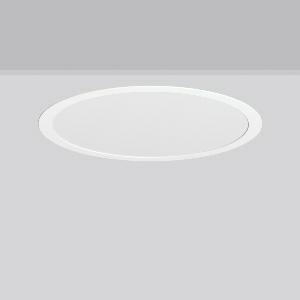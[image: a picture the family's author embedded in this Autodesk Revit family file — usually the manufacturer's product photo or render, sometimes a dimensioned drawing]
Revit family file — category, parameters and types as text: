
# Revit family: toledo_flat__round_e_901812_002_a753
name_source: partatom
category: Lighting Fixtures
units: mm (PartAtom-declared; Revit-internal decimal feet)

## family parameters
Cut with Voids When Loaded = No
Host = Face
Light Source = No
Part Type = Normal
Room Calculation Point = No
Round Connector Dimension = Use Diameter
Shared = No

## types (1)
- MultiLumen 1 (1 x LED Modul 840, 3050 lm, 4000)
    Apparent Load = 22 VA
    CIE Flux Codes = 47 79 96 100 100
    Color Rendering = 80
    Color Temperature = 4000
    Default Elevation = 1800 mm
    Description = Series: TOLEDO FLAT+ round
Flexible round recessed multifunction downlight. Housing: sheet steel, powder-coated. Luminaire frame: aluminium, powder-coated. Light guide and diffuser made of non-yellowing PMMA, opal matt. LED backlight technology for homogeneous illumination of the entire light-emitting surface. MultiColour: Colour temperature individually adjustable either 3000 K or 4000 K via switching element. Factory setting is 4000 K. MultiLumen: 4 steps adjustable luminous flux. Factory setting is step 2. Suitable for Recessed ceiling mounting. Ceiling installation with spring system. Can be directly covered with thermal insulation material (applies only to the lower lumen levels). Including separate LED converter with connecting cable 250 mm. Suitable for through-wiring with separately available accessories. Through-wiring box (5 pole) available as accessory. Surface mounted housing as accessory for all sizes. 
Colour: white
Diameter: 470 mm
Height: 2 mm
Cut-out diameter: 457 mm
Recess height: 70 mm
Luminaire: recess height: 41 mm
Lamp: LED
Socket: without socket
Colour temperature: 3000K, 4000K
Colour rendering index (CRI): 80
System power: 22 W
Rated luminous flux: 3050 lm
Luminous efficiency: 139 lm/W
System power 2: 26 W
Rated luminous flux 2: 3550 lm
Luminous efficiency 2: 137 lm/W
System power 3: 30 W
Rated luminous flux 3: 4000 lm
Luminous efficiency 3: 133 lm/W
System power 4: 33 W
Rated luminous flux 4: 4450 lm
Luminous efficiency 4: 135 lm/W
Control gear: Regulated power supply
Protection class: II
Type of protection: IP 54
    Height = 0 mm  [stored 0 ft]
    Lamp = 1 x LED Modul 840
    Lamp Light Flux = 3050 lm
    Lamp count = 1
    Length = 470 mm
    Lifetime = 50000 h
    Luminous efficacy = 139 lm/W
    Manufacturer = RZB
    ModVariant = No
    Model = 901812.002
    Mounting Place = Ceiling
    Mounting Type = Recessed
    Number of Poles = 1
    OnlyDefault = Yes
    Power Factor = 1
    Product Name = TOLEDO FLAT+ round E
    Product group = Recessed downlights
    ProductGroupID = 402
    Protection Class = Protection class II
    Protection Degree = Degree of protection
    RLX_Detail_Level = 1
    RLX_Emergency_Light_Flux = 0 lm
    RLX_Emergency_Type = 0
    RLX_Emergency_Type_DB = No
    RlxData = <blob elided: 35457 chars, md5=f4c89700>
    Socket = socket
    Standby Power = 0 W
    System Light Flux = 3050 lm
    System Power = 22 W
    Type Comments = MultiLumen 1
    Type Image = 901812.002.jpg
    URL = http://relux.com
    VarID = multilumen_1
    Voltage = 0 V
    Weight = 0.00 kg
    Width = 0 mm  [stored 0 ft]

note: [stored X ft] marks values corroborated as IEEE doubles in the binary element streams (Revit-internal decimal feet)

## geometry (parser evidence)
native form markers: Blend x4, Sweep x9
no freeform markers — native parametric forms only
